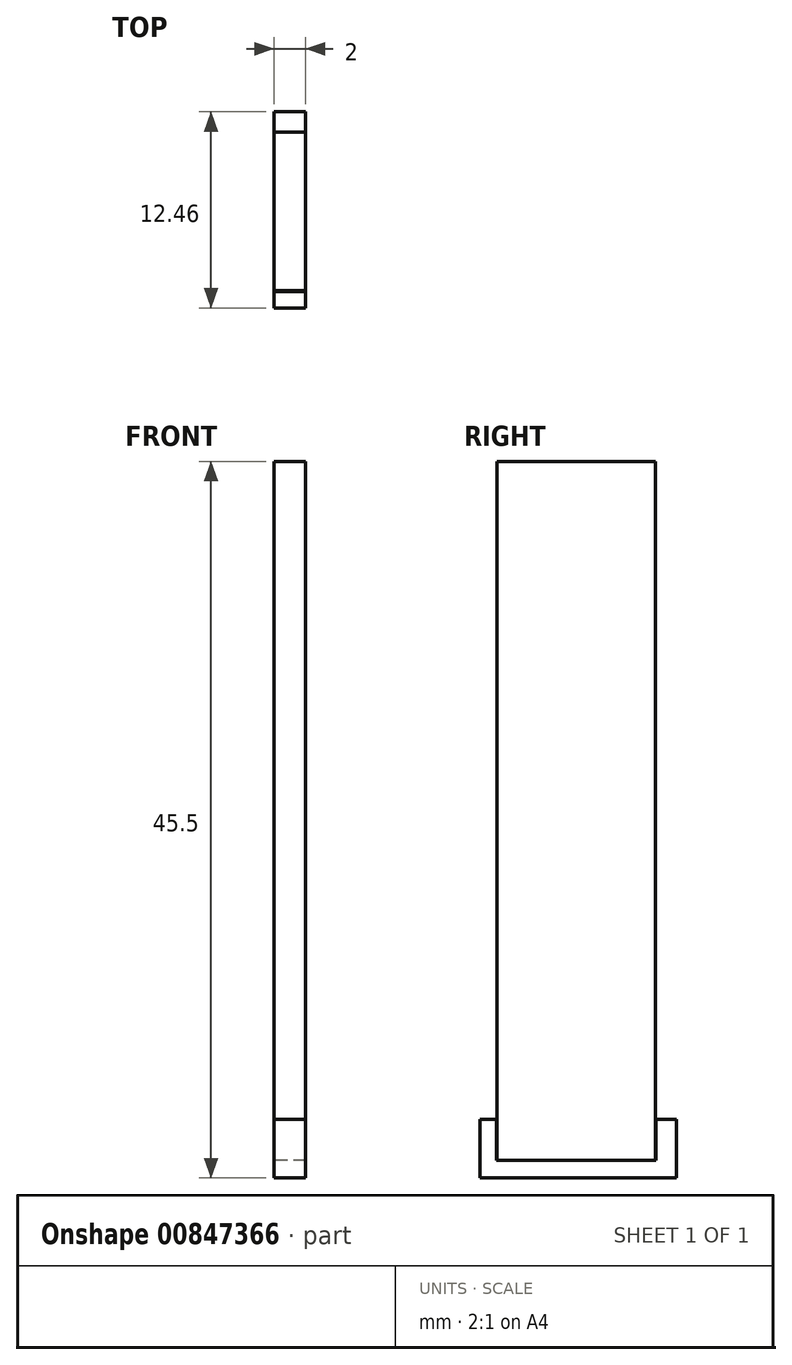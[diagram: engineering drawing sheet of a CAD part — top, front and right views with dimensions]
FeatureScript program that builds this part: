
annotation { "Feature Type Name" : "Feature", "Feature Type Description" : "" }
export const myFeature = defineFeature(function(context is Context, id is Id, definition is map)
    precondition{}
    {
        {
            var Q0;
            Q0=qCreatedBy(makeId("Right.planeOp"),FACE);
            var sketch = newSketch(context, id + "F0", { "sketchPlane" : qUnion([Q0])});
            skLineSegment(sketch, "E0.bottom", {"start": v(-6.9, 22.2) * mm, "end": v(3.17, 22.2) * mm});
            skLineSegment(sketch, "E0.top", {"start": v(-6.9, -22.2) * mm, "end": v(3.17, -22.2) * mm});
            skLineSegment(sketch, "E0.left", {"start": v(-6.9, 22.2) * mm, "end": v(-6.9, -22.2) * mm});
            skLineSegment(sketch, "E0.right", {"start": v(3.17, 22.2) * mm, "end": v(3.17, -22.2) * mm});
            skPoint(sketch, "E0.middle", {"position": v(-1.86, 0) * mm});
            skSolve(sketch);
        }
        {
            var Q0;
            Q0=makeQuery(id+"F0.imprint","IMPRINT",FACE,{"disambiguationData":[TD([[makeQuery(id+"F0.imprint","IMPRINT",EDGE,{"derivedFrom":sQuery(id+"F0.wireOp",EDGE,"E0.bottom")}),-1.0]])]});
            extrude(context, id + "F1", {"entities" : qUnion([Q0]), "depth" : 2 * mm, "offsetDistance" : 25 * mm});
        }
        {
            var Q0;
            Q0=qCreatedBy(makeId("Right.planeOp"),FACE);
            var sketch = newSketch(context, id + "F2", { "sketchPlane" : qUnion([Q0])});
            skLineSegment(sketch, "E1", {"start": v(-7.98, -19.58) * mm, "end": v(-6.93, -19.58) * mm});
            skLineSegment(sketch, "E2", {"start": v(4.48, -19.58) * mm, "end": v(4.48, -23.3) * mm});
            skLineSegment(sketch, "E3", {"start": v(4.48, -23.3) * mm, "end": v(-7.98, -23.3) * mm});
            skLineSegment(sketch, "E4", {"start": v(-7.98, -23.3) * mm, "end": v(-7.98, -19.58) * mm});
            skLineSegment(sketch, "E5", {"start": v(3.18, -19.58) * mm, "end": v(3.18, -22.2) * mm});
            skLineSegment(sketch, "E6", {"start": v(3.18, -22.2) * mm, "end": v(-6.93, -22.2) * mm});
            skLineSegment(sketch, "E7", {"start": v(-6.93, -22.2) * mm, "end": v(-6.93, -19.58) * mm});
            skLineSegment(sketch, "E8.trimOffspring", {"start": v(3.18, -19.58) * mm, "end": v(4.48, -19.58) * mm});
            skSolve(sketch);
        }
        {
            var Q0;
            Q0=makeQuery(id+"F2.imprint","IMPRINT",FACE,{"disambiguationData":[TD([[makeQuery(id+"F2.imprint","IMPRINT",EDGE,{"derivedFrom":sQuery(id+"F2.wireOp",EDGE,"E1")}),-1.0]])]});
            extrude(context, id + "F3", {"entities" : qUnion([Q0]), "depth" : 2 * mm, "offsetDistance" : 25 * mm});
        }
    });
